# Revit family: Скамейка для детских площадок «Палитра» Арт 10842
name_source: partatom
category: Антураж
revit_build: Autodesk Revit 2018 (Build: 20180423_1000(x64)
units: mm (PartAtom-declared; Revit-internal decimal feet)

## family parameters
Всегда вертикально = Да
Источник визуального образа = Геометрия семейства
На основе рабочей плоскости = Нет
Общий = Нет
При загрузке вырезать с полостями = Нет
Точка расчета площади = Нет

## types (2) — shared parameters
URL = https://hobbyka.ru
Артикул товара = Арт. 10842
Высота = 974 мм
Группа модели = Садовые скамейки
Длина = 1800 мм
Изготовитель = ООО «Хоббика»
Материал изделия = Дерево
Цвет лавки = Лавка
Цвет отделки = Спинка
Ширина = 630 мм

## per-type parameters (varying)
| type | Изображение типоразмера | Разноцветная | Стандарт |
| Скамейка для детских площадок «Палитра». Версия 1,8 м. Стандарт | Скамейка для детских площадок «Палитра» Арт 10842 Стандарт.jpg | Нет | Да |
| Скамейка для детских площадок «Палитра». Версия 1,8 м. Разноцветная | Скамейка для детских площадок «Палитра» Арт 10842 Разноцветная.jpeg | Да | Нет |

note: column(s) folded — value = type name in every type: Описание
